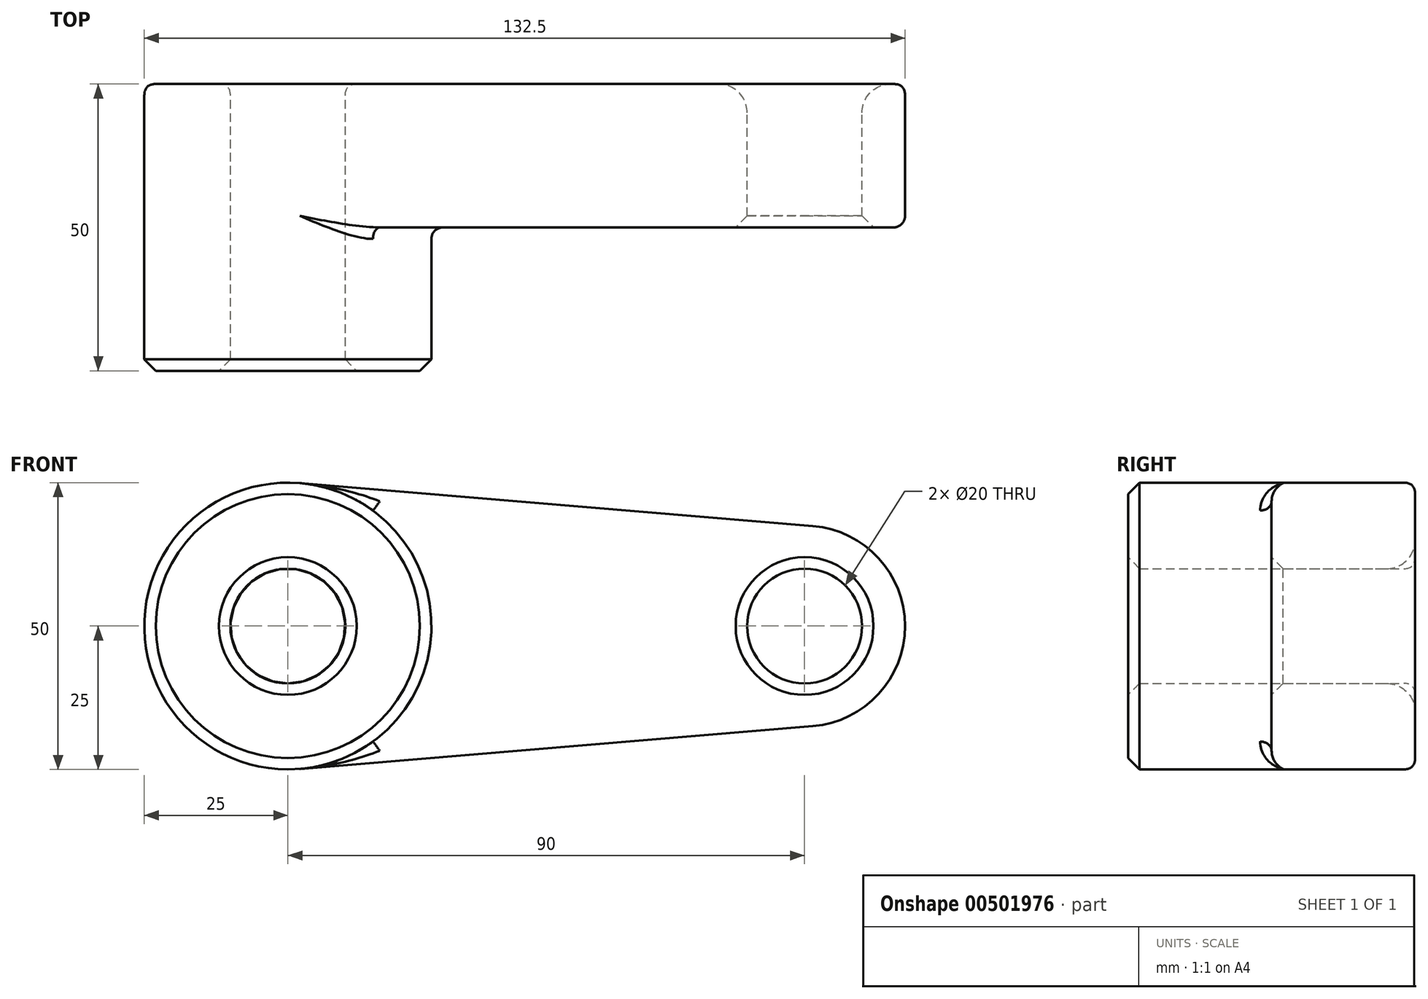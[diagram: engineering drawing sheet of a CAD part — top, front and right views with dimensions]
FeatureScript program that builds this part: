
annotation { "Feature Type Name" : "Feature", "Feature Type Description" : "" }
export const myFeature = defineFeature(function(context is Context, id is Id, definition is map)
    precondition{}
    {
        {
            var Q0;
            Q0=qCreatedBy(makeId("Front.planeOp"),FACE);
            var sketch = newSketch(context, id + "F0", { "sketchPlane" : qUnion([Q0])});
            skCircle(sketch, "E0", {"center": v(0, 0) * mm, "radius": 25 * mm});
            skCircle(sketch, "E1", {"center": v(90, 0) * mm, "radius": 17.5 * mm});
            skLineSegment(sketch, "E2", {"start": v(2.08, 24.91) * mm, "end": v(91.46, 17.44) * mm});
            skLineSegment(sketch, "E3", {"start": v(2.08, -24.91) * mm, "end": v(91.46, -17.44) * mm});
            skCircle(sketch, "E4", {"center": v(0, 0) * mm, "radius": 10 * mm});
            skCircle(sketch, "E5", {"center": v(90, 0) * mm, "radius": 10 * mm});
            skSolve(sketch);
        }
        {
            var Q0;
            Q0=qSketchRegion(id+"F0",true);
            extrude(context, id + "F1", {"entities" : qUnion([Q0]), "depth" : 25 * mm});
        }
        {
            var Q0;
            Q0=makeQuery(id+"F0.imprint","IMPRINT",FACE,{"disambiguationData":[TD([[makeQuery(id+"F0.imprint","IMPRINT",EDGE,{"derivedFrom":sQuery(id+"F0.wireOp",EDGE,"E4")}),-1.0]])]});
            extrude(context, id + "F2", {"entities" : qUnion([Q0]), "operationType" : NewBodyOperationType.ADD, "depth" : 50 * mm});
        }
        {
            var Q0;
            Q0=makeQuery(id+"F2.opExtrude","CAP_EDGE",EDGE,{"disambiguationData":[OSD([sQuery(id+"F0.wireOp",EDGE,"E0")])],"isStart":false});
            var Q1;
            Q1=makeQuery(id+"F2.opExtrude","CAP_EDGE",EDGE,{"disambiguationData":[OSD([sQuery(id+"F0.wireOp",EDGE,"E4")])],"isStart":false});
            var Q2;
            Q2=makeQuery(id+"F1.opExtrude","CAP_EDGE",EDGE,{"disambiguationData":[OSD([sQuery(id+"F0.wireOp",EDGE,"E5")])],"isStart":false});
            chamfer(context, id + "F3", {"entities" : qUnion([Q0, Q1, Q2]), "width" : 2 * mm, "tangentPropagation" : true});
        }
        {
            var Q0;
            Q0=makeQuery(id+"F1.opExtrude","CAP_EDGE",EDGE,{"disambiguationData":[OSD([sQuery(id+"F0.wireOp",EDGE,"E2")])],"isStart":true});
            var Q1;
            Q1=makeQuery(id+"F1.opExtrude","CAP_EDGE",EDGE,{"disambiguationData":[OSD([sQuery(id+"F0.wireOp",EDGE,"E4")])],"isStart":true});
            fillet(context, id + "F4", {"entities" : qUnion([Q0, Q1]), "radius" : 2 * mm, "tangentPropagation" : true, "rho" : 0.5, "crossSection" : FilletCrossSection.CONIC, "allowEdgeOverflow" : false});
        }
        {
            var Q0;
            Q0=makeQuery(id+"F1.opExtrude","CAP_EDGE",EDGE,{"disambiguationData":[OSD([sQuery(id+"F0.wireOp",EDGE,"E5")])],"isStart":true});
            fillet(context, id + "F5", {"entities" : qUnion([Q0]), "radius" : 5 * mm, "tangentPropagation" : true, "allowEdgeOverflow" : false});
        }
        {
            var Q0;
            {var subQ0=sQuery(id+"F0.wireOp",EDGE,"E0");Q0=makeQuery(id+"F2.boolean.opBoolean","INTERSECT",EDGE,{"derivedFrom":[makeQuery(id+"F1.opExtrude","CAP_FACE",FACE,{"disambiguationData":[OSD([subQ0,sQuery(id+"F0.wireOp",EDGE,"E1"),sQuery(id+"F0.wireOp",EDGE,"E2"),sQuery(id+"F0.wireOp",EDGE,"E3"),sQuery(id+"F0.wireOp",EDGE,"E4"),sQuery(id+"F0.wireOp",EDGE,"E5")])],"isStart":false}),makeQuery(id+"F2.opExtrude","SWEPT_FACE",FACE,{"disambiguationData":[OSD([subQ0])]})]});}
            var Q1;
            Q1=makeQuery(id+"F1.opExtrude","CAP_EDGE",EDGE,{"disambiguationData":[OSD([sQuery(id+"F0.wireOp",EDGE,"E2")])],"isStart":false});
            fillet(context, id + "F6", {"entities" : qUnion([Q0, Q1]), "radius" : 2 * mm, "tangentPropagation" : true, "allowEdgeOverflow" : false});
        }
    });
